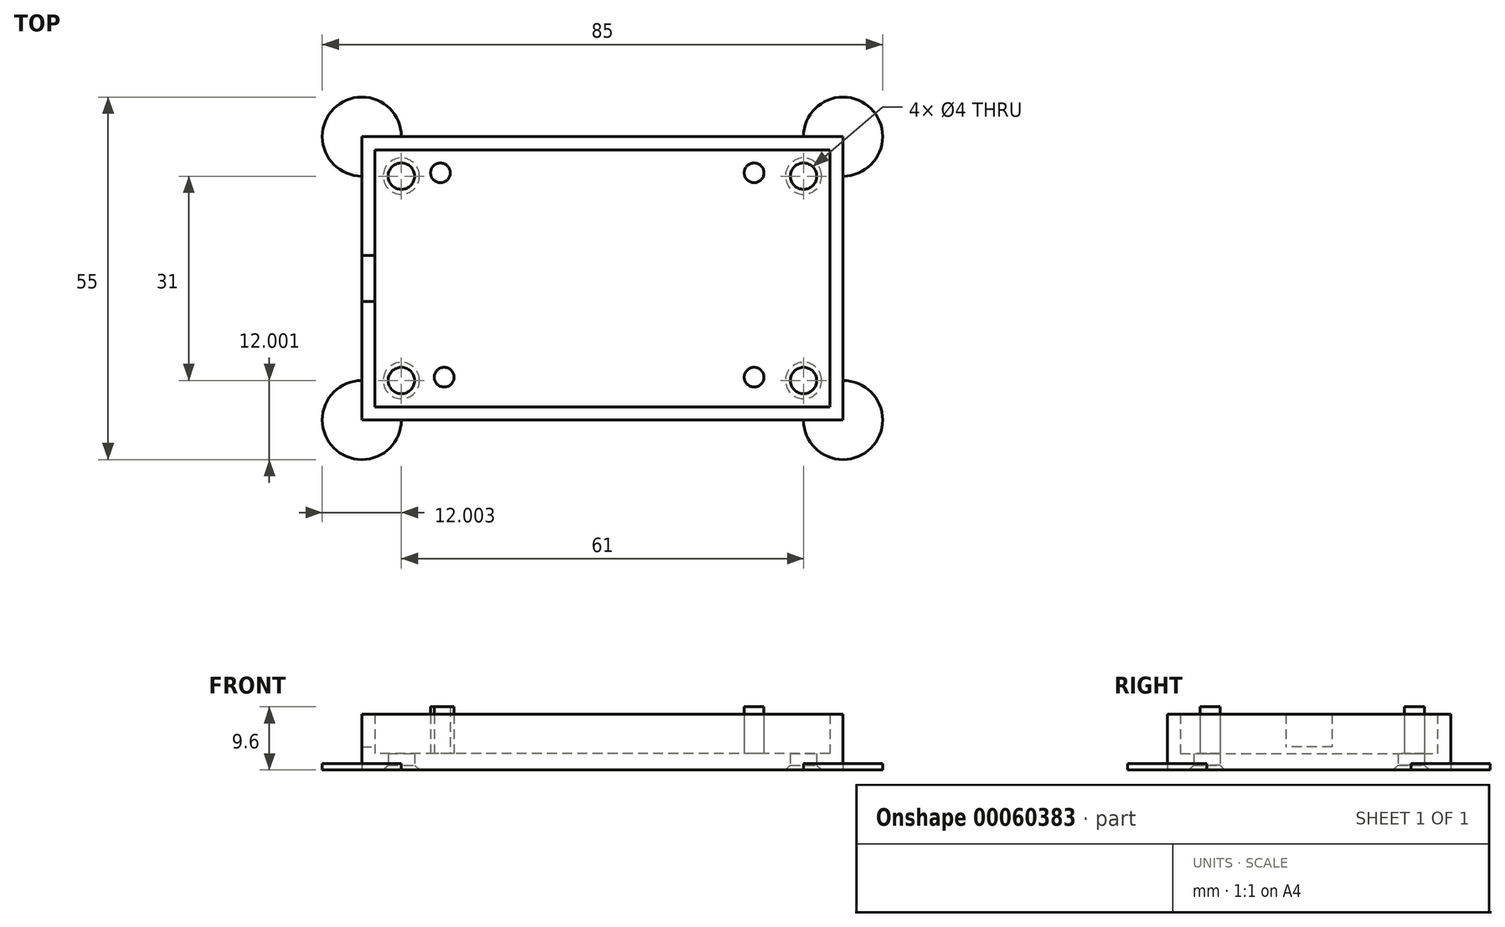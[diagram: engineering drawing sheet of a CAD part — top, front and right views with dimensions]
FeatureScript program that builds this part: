
annotation { "Feature Type Name" : "Feature", "Feature Type Description" : "" }
export const myFeature = defineFeature(function(context is Context, id is Id, definition is map)
    precondition{}
    {
        {
            var Q0;
            Q0=qCreatedBy(makeId("Top.planeOp"),FACE);
            var sketch = newSketch(context, id + "F0", { "sketchPlane" : qUnion([Q0])});
            skLineSegment(sketch, "E0.bottom", {"start": v(-11.76, 68.41) * mm, "end": v(57.24, 68.41) * mm});
            skLineSegment(sketch, "E0.top", {"start": v(-11.76, 29.41) * mm, "end": v(57.24, 29.41) * mm});
            skLineSegment(sketch, "E0.left", {"start": v(-11.76, 68.41) * mm, "end": v(-11.76, 29.41) * mm});
            skLineSegment(sketch, "E0.right", {"start": v(57.24, 68.41) * mm, "end": v(57.24, 29.41) * mm});
            skCircle(sketch, "E1", {"center": v(-7.76, 64.41) * mm, "radius": 1.5 * mm, "construction": true});
            skCircle(sketch, "E2", {"center": v(-7.76, 33.41) * mm, "radius": 1.5 * mm, "construction": true});
            skCircle(sketch, "E3", {"center": v(53.24, 64.41) * mm, "radius": 1.5 * mm, "construction": true});
            skCircle(sketch, "E4", {"center": v(53.24, 33.41) * mm, "radius": 1.5 * mm, "construction": true});
            skCircle(sketch, "E5.0", {"center": v(53.24, 33.41) * mm, "radius": 2 * mm});
            skCircle(sketch, "E6.0", {"center": v(53.24, 64.41) * mm, "radius": 2 * mm});
            skCircle(sketch, "E7.0", {"center": v(-7.76, 64.41) * mm, "radius": 2 * mm});
            skCircle(sketch, "E8.0", {"center": v(-7.76, 33.41) * mm, "radius": 2 * mm});
            skPoint(sketch, "E9", {"position": v(-1.26, 33.91) * mm});
            skLineSegment(sketch, "E10.0", {"start": v(-13.76, 70.41) * mm, "end": v(-13.76, 27.41) * mm});
            skLineSegment(sketch, "E10.1", {"start": v(-13.76, 70.41) * mm, "end": v(59.24, 70.41) * mm});
            skLineSegment(sketch, "E10.2", {"start": v(59.24, 70.41) * mm, "end": v(59.24, 27.41) * mm});
            skLineSegment(sketch, "E10.3", {"start": v(-13.76, 27.41) * mm, "end": v(59.24, 27.41) * mm});
            skPoint(sketch, "E11", {"position": v(-13.76, 52.41) * mm});
            skPoint(sketch, "E12", {"position": v(-13.76, 45.41) * mm});
            skLineSegment(sketch, "E13", {"start": v(-13.76, 52.41) * mm, "end": v(-11.76, 52.41) * mm});
            skLineSegment(sketch, "E14", {"start": v(-13.76, 45.41) * mm, "end": v(-11.76, 45.41) * mm});
            skPoint(sketch, "E15", {"position": v(-1.82, 64.91) * mm});
            skPoint(sketch, "E16", {"position": v(45.74, 33.91) * mm});
            skPoint(sketch, "E17", {"position": v(45.74, 64.91) * mm});
            skCircle(sketch, "E18", {"center": v(-1.26, 33.91) * mm, "radius": 1.5 * mm});
            skCircle(sketch, "E19", {"center": v(-1.82, 64.91) * mm, "radius": 1.5 * mm});
            skCircle(sketch, "E20", {"center": v(45.74, 64.91) * mm, "radius": 1.5 * mm});
            skCircle(sketch, "E21", {"center": v(45.74, 33.91) * mm, "radius": 1.5 * mm});
            skArc(sketch, "E22", {"start": v(59.24, 64.41) * mm, "mid": v(63.49, 74.65) * mm, "end": v(53.24, 70.41) * mm});
            skArc(sketch, "E23", {"start": v(53.24, 27.41) * mm, "mid": v(63.49, 23.17) * mm, "end": v(59.24, 33.41) * mm});
            skArc(sketch, "E24", {"start": v(-7.76, 70.41) * mm, "mid": v(-18, 74.65) * mm, "end": v(-13.76, 64.41) * mm});
            skArc(sketch, "E25", {"start": v(-13.76, 33.41) * mm, "mid": v(-18, 23.17) * mm, "end": v(-7.76, 27.41) * mm});
            skSolve(sketch);
        }
        {
            var Q0;
            {var subQ0=sQuery(id+"F0.wireOp",EDGE,"E0.bottom");Q0=makeQuery(id+"F0.imprint","IMPRINT",FACE,{"disambiguationData":[TD([[makeQuery(id+"F0.imprint","IMPRINT",EDGE,{"derivedFrom":subQ0}),-1.0]])]});}
            var Q1;
            {var subQ5=sQuery(id+"F0.wireOp",EDGE,"E0.bottom");Q1=makeQuery(id+"F0.imprint","IMPRINT",FACE,{"disambiguationData":[TD([[makeQuery(id+"F0.imprint","IMPRINT",EDGE,{"derivedFrom":subQ5}),1.0]])]});}
            var Q2;
            Q2=makeQuery(id+"F0.imprint","IMPRINT",FACE,{"disambiguationData":[TD([[makeQuery(id+"F0.imprint","IMPRINT",EDGE,{"derivedFrom":sQuery(id+"F0.wireOp",EDGE,"E18")}),1.0]])]});
            var Q3;
            Q3=makeQuery(id+"F0.imprint","IMPRINT",FACE,{"disambiguationData":[TD([[makeQuery(id+"F0.imprint","IMPRINT",EDGE,{"derivedFrom":sQuery(id+"F0.wireOp",EDGE,"E21")}),1.0]])]});
            var Q4;
            Q4=makeQuery(id+"F0.imprint","IMPRINT",FACE,{"disambiguationData":[TD([[makeQuery(id+"F0.imprint","IMPRINT",EDGE,{"derivedFrom":sQuery(id+"F0.wireOp",EDGE,"E20")}),1.0]])]});
            var Q5;
            Q5=makeQuery(id+"F0.imprint","IMPRINT",FACE,{"disambiguationData":[TD([[makeQuery(id+"F0.imprint","IMPRINT",EDGE,{"derivedFrom":sQuery(id+"F0.wireOp",EDGE,"E19")}),1.0]])]});
            var Q6;
            {var subQ0=sQuery(id+"F0.wireOp",EDGE,"E13");Q6=makeQuery(id+"F0.imprint","IMPRINT",FACE,{"disambiguationData":[TD([[makeQuery(id+"F0.imprint","IMPRINT",EDGE,{"derivedFrom":subQ0}),-1.0]])]});}
            extrude(context, id + "F1", {"entities" : qUnion([Q0, Q1, Q2, Q3, Q4, Q5, Q6]), "depth" : 2.5 * mm});
        }
        {
            var Q0;
            {var subQ5=sQuery(id+"F0.wireOp",EDGE,"E0.bottom");Q0=makeQuery(id+"F0.imprint","IMPRINT",FACE,{"disambiguationData":[TD([[makeQuery(id+"F0.imprint","IMPRINT",EDGE,{"derivedFrom":subQ5}),1.0]])]});}
            extrude(context, id + "F2", {"entities" : qUnion([Q0]), "operationType" : NewBodyOperationType.ADD, "depth" : 8.5 * mm});
        }
        {
            var Q0;
            Q0=makeQuery(id+"F0.imprint","IMPRINT",FACE,{"disambiguationData":[TD([[makeQuery(id+"F0.imprint","IMPRINT",EDGE,{"derivedFrom":sQuery(id+"F0.wireOp",EDGE,"E19")}),1.0]])]});
            var Q1;
            Q1=makeQuery(id+"F0.imprint","IMPRINT",FACE,{"disambiguationData":[TD([[makeQuery(id+"F0.imprint","IMPRINT",EDGE,{"derivedFrom":sQuery(id+"F0.wireOp",EDGE,"E18")}),1.0]])]});
            var Q2;
            Q2=makeQuery(id+"F0.imprint","IMPRINT",FACE,{"disambiguationData":[TD([[makeQuery(id+"F0.imprint","IMPRINT",EDGE,{"derivedFrom":sQuery(id+"F0.wireOp",EDGE,"E21")}),1.0]])]});
            var Q3;
            Q3=makeQuery(id+"F0.imprint","IMPRINT",FACE,{"disambiguationData":[TD([[makeQuery(id+"F0.imprint","IMPRINT",EDGE,{"derivedFrom":sQuery(id+"F0.wireOp",EDGE,"E20")}),1.0]])]});
            extrude(context, id + "F3", {"entities" : qUnion([Q0, Q1, Q2, Q3]), "operationType" : NewBodyOperationType.ADD, "depth" : 9.6 * mm});
        }
        {
            var Q0;
            {var subQ0=sQuery(id+"F0.wireOp",EDGE,"E13");Q0=makeQuery(id+"F0.imprint","IMPRINT",FACE,{"disambiguationData":[TD([[makeQuery(id+"F0.imprint","IMPRINT",EDGE,{"derivedFrom":subQ0}),-1.0]])]});}
            extrude(context, id + "F4", {"entities" : qUnion([Q0]), "operationType" : NewBodyOperationType.ADD, "depth" : 3.5 * mm});
        }
        {
            var Q0;
            Q0=sQuery(id+"F0.wireOp",VERTEX,"E3.center");
            var Q1;
            Q1=sQuery(id+"F0.wireOp",VERTEX,"E4.center");
            var Q2;
            Q2=sQuery(id+"F0.wireOp",VERTEX,"E2.center");
            var Q3;
            Q3=sQuery(id+"F0.wireOp",VERTEX,"E1.center");
            var Q4;
            Q4=makeQuery(id+"F1.opExtrude","SWEPT_BODY",BODY,{"disambiguationData":[OSD([sQuery(id+"F0.wireOp",EDGE,"E5.0"),sQuery(id+"F0.wireOp",EDGE,"E6.0"),sQuery(id+"F0.wireOp",EDGE,"E7.0"),sQuery(id+"F0.wireOp",EDGE,"E8.0"),sQuery(id+"F0.wireOp",EDGE,"E10.0"),sQuery(id+"F0.wireOp",EDGE,"E10.1"),sQuery(id+"F0.wireOp",EDGE,"E10.2"),sQuery(id+"F0.wireOp",EDGE,"E10.3")])]});
            hole(context, id + "F5", {"style" : HoleStyle.C_SINK, "holeDiameter" : 3 * mm, "cSinkDiameter" : 5.5 * mm, "endStyle" : HoleEndStyle.THROUGH, "oppositeDirection" : true, "locations" : qUnion([Q0, Q1, Q2, Q3]), "scope" : qUnion([Q4]), "cSinkAngle" : 90 * degree});
        }
        {
            var Q0;
            {var subQ3=sQuery(id+"F0.wireOp",EDGE,"E24");Q0=makeQuery(id+"F0.imprint","IMPRINT",FACE,{"disambiguationData":[TD([[makeQuery(id+"F0.imprint","IMPRINT",EDGE,{"derivedFrom":subQ3}),1.0]])]});}
            var Q1;
            {var subQ3=sQuery(id+"F0.wireOp",EDGE,"E22");Q1=makeQuery(id+"F0.imprint","IMPRINT",FACE,{"disambiguationData":[TD([[makeQuery(id+"F0.imprint","IMPRINT",EDGE,{"derivedFrom":subQ3}),1.0]])]});}
            var Q2;
            {var subQ3=sQuery(id+"F0.wireOp",EDGE,"E23");Q2=makeQuery(id+"F0.imprint","IMPRINT",FACE,{"disambiguationData":[TD([[makeQuery(id+"F0.imprint","IMPRINT",EDGE,{"derivedFrom":subQ3}),1.0]])]});}
            var Q3;
            {var subQ3=sQuery(id+"F0.wireOp",EDGE,"E25");Q3=makeQuery(id+"F0.imprint","IMPRINT",FACE,{"disambiguationData":[TD([[makeQuery(id+"F0.imprint","IMPRINT",EDGE,{"derivedFrom":subQ3}),1.0]])]});}
            extrude(context, id + "F6", {"entities" : qUnion([Q0, Q1, Q2, Q3]), "operationType" : NewBodyOperationType.ADD, "depth" : 1 * mm});
        }
    });
